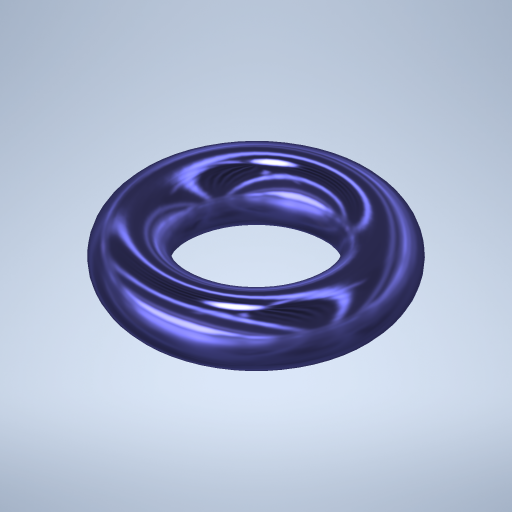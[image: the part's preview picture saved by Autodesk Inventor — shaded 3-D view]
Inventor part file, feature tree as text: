
AUTODESK INVENTOR PART (.ipt)
format: ipt  version: 2023.1 (Build 271208000, 208)  size: 358,400 bytes
history: native  units: in
note: dims shown in document units (in); Inventor stores cm internally (conversion verified against a paired STEP export)
features: plane x2, revolve x1, sketch x1
ambient origin geometry x8: Origin, YZ Plane, XZ Plane, XY Plane, X Axis, Y Axis, Z Axis, Center Point
bodies: Solid1 (feature_tree)
feature tree (4):
  revolve  "Revolution1"  [1 undecoded]
  plane  "Work Plane1"
  plane  "Work Plane2"
  sketch  "Sketch1"  dims[d0=0.0625in d1=0.0938in d2=90.0deg d3=0.0312in d4=-0.0312in]
note: 1 required parameter value undecoded (feature->parameter linkage not recoverable at this tier; creation-order binding heuristic only, values carry confidence <= 0.55)
